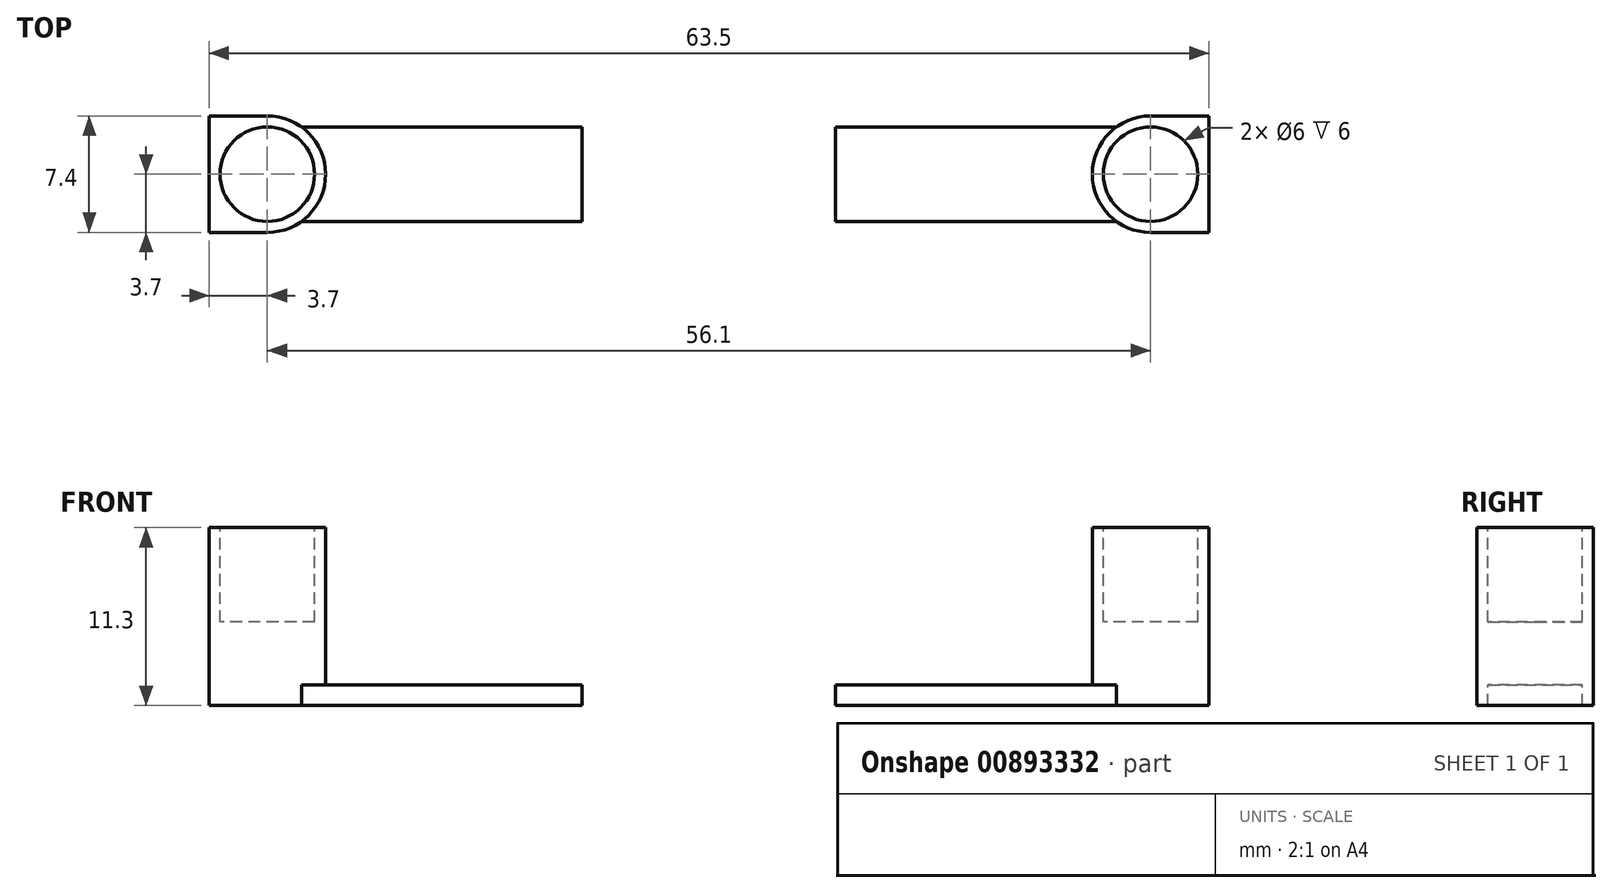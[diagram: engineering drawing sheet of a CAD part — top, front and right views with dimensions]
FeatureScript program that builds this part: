
annotation { "Feature Type Name" : "Feature", "Feature Type Description" : "" }
export const myFeature = defineFeature(function(context is Context, id is Id, definition is map)
    precondition{}
    {
        {
            var Q0;
            Q0=qCreatedBy(makeId("Top.planeOp"),FACE);
            var sketch = newSketch(context, id + "F0", { "sketchPlane" : qUnion([Q0])});
            skLineSegment(sketch, "E0.bottom", {"start": v(0, 0) * mm, "end": v(63.5, 0) * mm});
            skLineSegment(sketch, "E0.top", {"start": v(0, 7.4) * mm, "end": v(63.5, 7.4) * mm});
            skLineSegment(sketch, "E0.left", {"start": v(0, 0) * mm, "end": v(0, 7.4) * mm});
            skLineSegment(sketch, "E0.right", {"start": v(63.5, 0) * mm, "end": v(63.5, 7.4) * mm});
            skLineSegment(sketch, "E1", {"start": v(-15.24, 3.7) * mm, "end": v(83.2, 3.7) * mm, "construction": true});
            skCircle(sketch, "E2", {"center": v(3.7, 3.7) * mm, "radius": 3 * mm});
            skCircle(sketch, "E3", {"center": v(59.8, 3.7) * mm, "radius": 3 * mm});
            skLineSegment(sketch, "E4", {"start": v(3.7, 3.7) * mm, "end": v(3.7, 0) * mm, "construction": true});
            skLineSegment(sketch, "E5", {"start": v(3.7, 0) * mm, "end": v(3.7, 3.7) * mm, "construction": true});
            skLineSegment(sketch, "E6", {"start": v(3.7, 7.4) * mm, "end": v(3.7, 3.7) * mm, "construction": true});
            skLineSegment(sketch, "E7", {"start": v(59.8, 3.7) * mm, "end": v(59.8, 7.4) * mm, "construction": true});
            skLineSegment(sketch, "E8", {"start": v(59.8, 7.4) * mm, "end": v(59.8, 0) * mm, "construction": true});
            skLineSegment(sketch, "E9", {"start": v(3.7, 6.7) * mm, "end": v(59.8, 6.7) * mm});
            skLineSegment(sketch, "E10", {"start": v(59.8, 0.7) * mm, "end": v(3.7, 0.7) * mm});
            skPoint(sketch, "E10.endSnap0", {"position": v(3.7, 1.85) * mm});
            skLineSegment(sketch, "E11.bottom", {"start": v(23.7, 6.7) * mm, "end": v(39.8, 6.7) * mm});
            skLineSegment(sketch, "E11.top", {"start": v(23.7, 0.7) * mm, "end": v(39.8, 0.7) * mm});
            skLineSegment(sketch, "E11.left", {"start": v(23.7, 6.7) * mm, "end": v(23.7, 0.7) * mm});
            skLineSegment(sketch, "E11.right", {"start": v(39.8, 6.7) * mm, "end": v(39.8, 0.7) * mm});
            skCircle(sketch, "E12", {"center": v(3.7, 3.7) * mm, "radius": 3.7 * mm});
            skCircle(sketch, "E13", {"center": v(59.8, 3.7) * mm, "radius": 3.7 * mm});
            skSolve(sketch);
        }
        {
            var Q0;
            {var subQ0=sQuery(id+"F0.wireOp",EDGE,"E11.bottom");Q0=makeQuery(id+"F0.imprint","IMPRINT",FACE,{"disambiguationData":[TD([[makeQuery(id+"F0.imprint","IMPRINT",EDGE,{"derivedFrom":subQ0}),1.0]])]});}
            var Q1;
            {var subQ3=sQuery(id+"F0.wireOp",EDGE,"E9");var subQ4=sQuery(id+"F0.wireOp",EDGE,"E3");var subQ5=makeQuery(id+"F0.imprint","INTERSECT",VERTEX,{"derivedFrom":[subQ4,subQ3]});Q1=makeQuery(id+"F0.imprint","IMPRINT",FACE,{"disambiguationData":[TD([[makeQuery(id+"F0.imprint","IMPRINT",EDGE,{"disambiguationData":[TD([[subQ5,1.0]])],"derivedFrom":subQ4}),-1.0]])]});}
            var Q2;
            {var subQ0=sQuery(id+"F0.wireOp",EDGE,"E0.right");var subQ1=sQuery(id+"F0.wireOp",EDGE,"E0.top");var subQ2=makeQuery(id+"F0.imprint","INTERSECT",VERTEX,{"derivedFrom":[subQ1,subQ0]});Q2=makeQuery(id+"F0.imprint","IMPRINT",FACE,{"disambiguationData":[TD([[makeQuery(id+"F0.imprint","IMPRINT",EDGE,{"disambiguationData":[TD([[subQ2,1.0]])],"derivedFrom":subQ1}),-1.0]])]});}
            var Q3;
            {var subQ0=sQuery(id+"F0.wireOp",EDGE,"E0.right");var subQ1=sQuery(id+"F0.wireOp",EDGE,"E0.bottom");var subQ2=makeQuery(id+"F0.imprint","INTERSECT",VERTEX,{"derivedFrom":[subQ1,subQ0]});Q3=makeQuery(id+"F0.imprint","IMPRINT",FACE,{"disambiguationData":[TD([[makeQuery(id+"F0.imprint","IMPRINT",EDGE,{"disambiguationData":[TD([[subQ2,1.0]])],"derivedFrom":subQ1}),1.0]])]});}
            var Q4;
            {var subQ0=sQuery(id+"F0.wireOp",EDGE,"E11.top");Q4=makeQuery(id+"F0.imprint","IMPRINT",FACE,{"disambiguationData":[TD([[makeQuery(id+"F0.imprint","IMPRINT",EDGE,{"derivedFrom":subQ0}),-1.0]])]});}
            var Q5;
            {var subQ0=sQuery(id+"F0.wireOp",EDGE,"E9");var subQ1=sQuery(id+"F0.wireOp",EDGE,"E3");var subQ2=makeQuery(id+"F0.imprint","INTERSECT",VERTEX,{"derivedFrom":[subQ1,subQ0]});Q5=makeQuery(id+"F0.imprint","IMPRINT",FACE,{"disambiguationData":[TD([[makeQuery(id+"F0.imprint","IMPRINT",EDGE,{"disambiguationData":[TD([[subQ2,-1.0]])],"derivedFrom":subQ1}),-1.0]])]});}
            var Q6;
            Q6=makeQuery(id+"F0.imprint","IMPRINT",FACE,{"disambiguationData":[TD([[makeQuery(id+"F0.imprint","IMPRINT",EDGE,{"derivedFrom":sQuery(id+"F0.wireOp",EDGE,"E11.bottom")}),-1.0]])]});
            var Q7;
            {var subQ0=sQuery(id+"F0.wireOp",EDGE,"E9");var subQ1=sQuery(id+"F0.wireOp",EDGE,"E2");var subQ2=makeQuery(id+"F0.imprint","INTERSECT",VERTEX,{"derivedFrom":[subQ1,subQ0]});Q7=makeQuery(id+"F0.imprint","IMPRINT",FACE,{"disambiguationData":[TD([[makeQuery(id+"F0.imprint","IMPRINT",EDGE,{"disambiguationData":[TD([[subQ2,1.0]])],"derivedFrom":subQ1}),-1.0]])]});}
            var Q8;
            {var subQ2=sQuery(id+"F0.wireOp",EDGE,"E9");var subQ5=sQuery(id+"F0.wireOp",EDGE,"E2");var subQ8=makeQuery(id+"F0.imprint","INTERSECT",VERTEX,{"derivedFrom":[subQ5,subQ2]});Q8=makeQuery(id+"F0.imprint","IMPRINT",FACE,{"disambiguationData":[TD([[makeQuery(id+"F0.imprint","IMPRINT",EDGE,{"disambiguationData":[TD([[subQ8,-1.0]])],"derivedFrom":subQ5}),-1.0]])]});}
            var Q9;
            {var subQ0=sQuery(id+"F0.wireOp",EDGE,"E0.left");var subQ1=sQuery(id+"F0.wireOp",EDGE,"E0.top");var subQ2=makeQuery(id+"F0.imprint","INTERSECT",VERTEX,{"derivedFrom":[subQ1,subQ0]});Q9=makeQuery(id+"F0.imprint","IMPRINT",FACE,{"disambiguationData":[TD([[makeQuery(id+"F0.imprint","IMPRINT",EDGE,{"disambiguationData":[TD([[subQ2,-1.0]])],"derivedFrom":subQ1}),-1.0]])]});}
            var Q10;
            {var subQ0=sQuery(id+"F0.wireOp",EDGE,"E0.left");var subQ1=sQuery(id+"F0.wireOp",EDGE,"E0.bottom");var subQ2=makeQuery(id+"F0.imprint","INTERSECT",VERTEX,{"derivedFrom":[subQ1,subQ0]});Q10=makeQuery(id+"F0.imprint","IMPRINT",FACE,{"disambiguationData":[TD([[makeQuery(id+"F0.imprint","IMPRINT",EDGE,{"disambiguationData":[TD([[subQ2,-1.0]])],"derivedFrom":subQ1}),1.0]])]});}
            var Q11;
            {var subQ0=sQuery(id+"F0.wireOp",EDGE,"E2");var subQ1=makeQuery(id+"F0.imprint","INTERSECT",VERTEX,{"derivedFrom":[subQ0,sQuery(id+"F0.wireOp",EDGE,"E9")]});Q11=makeQuery(id+"F0.imprint","IMPRINT",FACE,{"disambiguationData":[TD([[makeQuery(id+"F0.imprint","IMPRINT",EDGE,{"disambiguationData":[TD([[subQ1,-1.0]])],"derivedFrom":subQ0}),1.0]])]});}
            var Q12;
            {var subQ0=sQuery(id+"F0.wireOp",EDGE,"E11.left");Q12=makeQuery(id+"F0.imprint","IMPRINT",FACE,{"disambiguationData":[TD([[makeQuery(id+"F0.imprint","IMPRINT",EDGE,{"derivedFrom":subQ0}),-1.0]])]});}
            var Q13;
            {var subQ0=sQuery(id+"F0.wireOp",EDGE,"E11.right");Q13=makeQuery(id+"F0.imprint","IMPRINT",FACE,{"disambiguationData":[TD([[makeQuery(id+"F0.imprint","IMPRINT",EDGE,{"derivedFrom":subQ0}),1.0]])]});}
            var Q14;
            {var subQ0=sQuery(id+"F0.wireOp",EDGE,"E3");var subQ1=makeQuery(id+"F0.imprint","INTERSECT",VERTEX,{"derivedFrom":[subQ0,sQuery(id+"F0.wireOp",EDGE,"E9")]});Q14=makeQuery(id+"F0.imprint","IMPRINT",FACE,{"disambiguationData":[TD([[makeQuery(id+"F0.imprint","IMPRINT",EDGE,{"disambiguationData":[TD([[subQ1,-1.0]])],"derivedFrom":subQ0}),1.0]])]});}
            extrude(context, id + "F1", {"entities" : qUnion([Q0, Q1, Q2, Q3, Q4, Q5, Q6, Q7, Q8, Q9, Q10, Q11, Q12, Q13, Q14]), "oppositeDirection" : true, "depth" : 11.3 * mm, "offsetDistance" : 25 * mm});
        }
        {
            var Q0;
            {var subQ0=sQuery(id+"F0.wireOp",EDGE,"E2");var subQ1=makeQuery(id+"F0.imprint","INTERSECT",VERTEX,{"derivedFrom":[subQ0,sQuery(id+"F0.wireOp",EDGE,"E9")]});Q0=makeQuery(id+"F0.imprint","IMPRINT",FACE,{"disambiguationData":[TD([[makeQuery(id+"F0.imprint","IMPRINT",EDGE,{"disambiguationData":[TD([[subQ1,-1.0]])],"derivedFrom":subQ0}),1.0]])]});}
            var Q1;
            {var subQ0=sQuery(id+"F0.wireOp",EDGE,"E3");var subQ1=makeQuery(id+"F0.imprint","INTERSECT",VERTEX,{"derivedFrom":[subQ0,sQuery(id+"F0.wireOp",EDGE,"E9")]});Q1=makeQuery(id+"F0.imprint","IMPRINT",FACE,{"disambiguationData":[TD([[makeQuery(id+"F0.imprint","IMPRINT",EDGE,{"disambiguationData":[TD([[subQ1,-1.0]])],"derivedFrom":subQ0}),1.0]])]});}
            extrude(context, id + "F2", {"entities" : qUnion([Q0, Q1]), "operationType" : NewBodyOperationType.REMOVE, "oppositeDirection" : true, "depth" : 6 * mm, "offsetDistance" : 25 * mm});
        }
        {
            var Q0;
            {var subQ0=sQuery(id+"F0.wireOp",EDGE,"E11.left");Q0=makeQuery(id+"F0.imprint","IMPRINT",FACE,{"disambiguationData":[TD([[makeQuery(id+"F0.imprint","IMPRINT",EDGE,{"derivedFrom":subQ0}),-1.0]])]});}
            var Q1;
            {var subQ0=sQuery(id+"F0.wireOp",EDGE,"E11.right");Q1=makeQuery(id+"F0.imprint","IMPRINT",FACE,{"disambiguationData":[TD([[makeQuery(id+"F0.imprint","IMPRINT",EDGE,{"derivedFrom":subQ0}),1.0]])]});}
            extrude(context, id + "F3", {"entities" : qUnion([Q0, Q1]), "operationType" : NewBodyOperationType.REMOVE, "oppositeDirection" : true, "depth" : 10 * mm, "offsetDistance" : 25 * mm});
        }
    });
